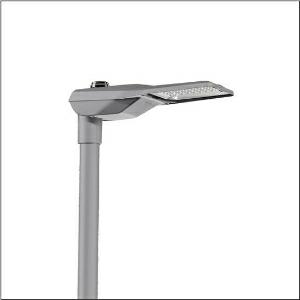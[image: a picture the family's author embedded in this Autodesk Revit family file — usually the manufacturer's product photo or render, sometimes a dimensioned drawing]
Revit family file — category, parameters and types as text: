
# Revit family: streetlight_sl_21_mini___st0_8a_5xe6c47n08jb_51ba
name_source: partatom
category: Lighting Fixtures
units: mm (PartAtom-declared; Revit-internal decimal feet)

## family parameters
Cut with Voids When Loaded = No
Host = Face
Light Source = No
Part Type = Normal
Room Calculation Point = No
Round Connector Dimension = Use Diameter
Shared = No

## types (1)
- --- (1 x LED, 13390 lm, 87.3 W, 4000K)
    Apparent Load = 87 VA
    CIE Flux Codes = 41 75 97 100 100
    Color Rendering = 70
    Color Temperature = 4000K
    Default Elevation = 1800 mm
    Description = Streetlight SL 21 mini, mast luminaire, primary light control with lens, of PMMA, primary optical cover: cover, of toughened safety glass, transparent, light distribution: ST0.8a, light emission: direct distribution, primary light characteristic: asymmetric, installation type: side-entry, LED, 3G 2.5mm², High Power LED, rated luminous flux: 13.390lm, luminous efficacy: 153lm/W, light colour: 740, colour temperature: 4000K, control gear: NEMA (7pin), control: overheat protection, pre-setting: linear dimming characteristic, constant luminous flux control, time-dependent luminous flux control, flexible luminous flux parameterisation, mains connection: 230..240V, AC, 50/60Hz, connection cable pre-assembled, cable length: 10,5m, wiring characteristics: H05VV-F, start of lifetime: 87W, end of service life: 90W, reduction: 40W, luminaire housing, of diecast aluminium (EN AC-44300), powder-coated, Siteco® metallic grey (DB 702S), corrosivity category C5 mid according to DIN EN ISO 12944, multi-level sealing system, sealing non-destructively replaceable, inclination adjustable: 0°, 5°, 10°, 15°, length: 628mm, width: 235mm, height: 110mm, spigot size: 42mm (side-entry), mounting height: 4..8m, protection rating (complete): IP66, insulation class (complete): insulation class I (protective earthing), certification: CE, ENEC, ENEC+, VDE, impact resistance: IK10, permissible operating ambient temperature for outdoor applications: -40..+50°C, standard-compliant lighting for roads and squares, packaging unit: 1 piece

Light Distribution: ST0.8a
    Height = 110 mm
    Lamp = 1 x LED
    Lamp Light Flux = 13390 lm
    Lamp Power = 87.3 W
    Lamp count = 1
    Length = 625 mm
    Luminous efficacy = 153 lm/W
    Manufacturer = Siteco
    ModVariant = No
    Model = 5XE6C47N08JB
    Number of Poles = 1
    OnlyDefault = Yes
    Power Factor = 1
    Product Name = Streetlight SL 21 mini | ST0.8a
    Product group = mast luminaire | pylon top
    ProductGroupID = 6100
    Protection Class = Protection class I
    Protection Degree = IP 66
    RLX_Detail_Level = 1
    RLX_Emergency_Light_Flux = 0 lm
    RLX_Emergency_Type = 0
    RLX_Emergency_Type_DB = No
    RlxData = <blob elided: 26085 chars, md5=a5d46cf5>
    Socket = socket
    Standby Power = 0 W
    System Light Flux = 13390 lm
    System Power = 87 W
    Type Comments = factory setting: luminous flux: 100 % | dim-lin: 254 | 915 mA
    Type Image = l_1294379.jpg
    URL = http://relux.com
    VarID = @adj_133912
    Voltage = 0 V
    Weight = 0.00 kg
    Width = 234 mm

## geometry (parser evidence)
native form markers: Blend x4, Sweep x9
no freeform markers — native parametric forms only
